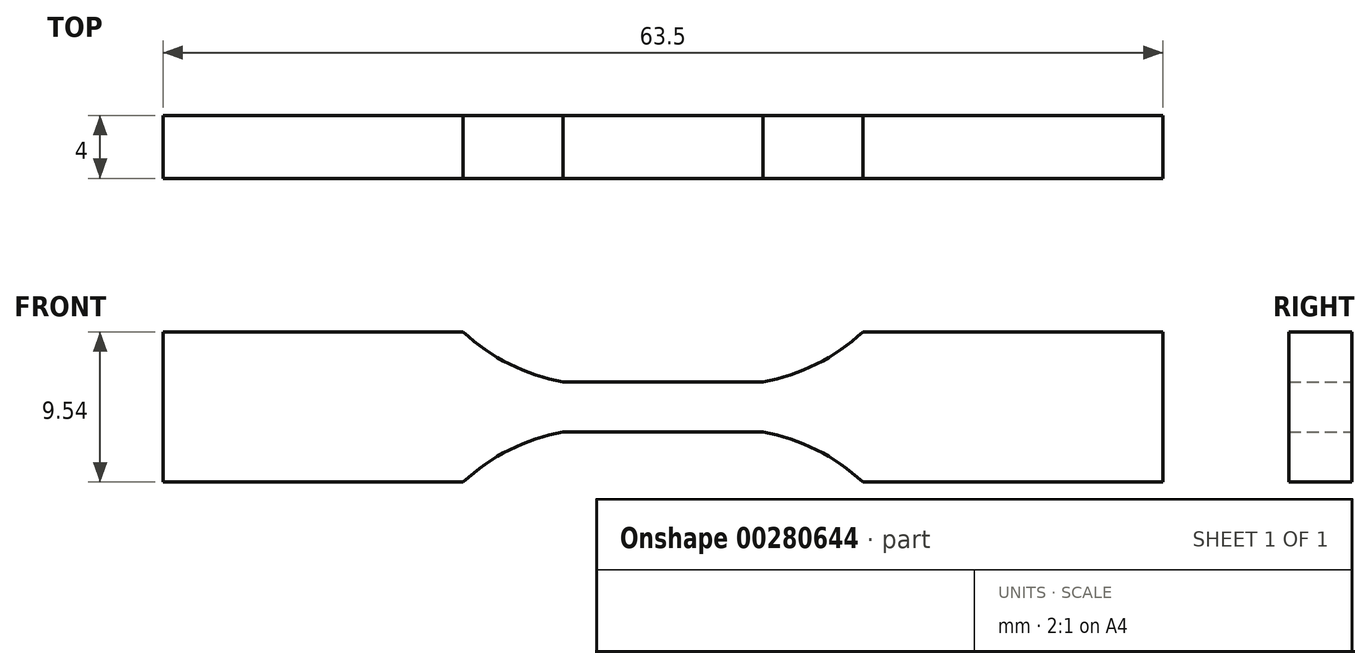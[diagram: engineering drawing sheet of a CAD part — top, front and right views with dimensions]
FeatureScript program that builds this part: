
annotation { "Feature Type Name" : "Feature", "Feature Type Description" : "" }
export const myFeature = defineFeature(function(context is Context, id is Id, definition is map)
    precondition{}
    {
        {
            var Q0;
            Q0=qCreatedBy(makeId("Front.planeOp"),FACE);
            var sketch = newSketch(context, id + "F0", { "sketchPlane" : qUnion([Q0])});
            skLineSegment(sketch, "E0", {"start": v(0, 1.6) * mm, "end": v(6.35, 1.6) * mm});
            skArc(sketch, "E1", {"start": v(6.35, 1.59) * mm, "mid": v(9.75, 2.72) * mm, "end": v(12.7, 4.76) * mm});
            skLineSegment(sketch, "E2", {"start": v(12.7, 4.76) * mm, "end": v(31.75, 4.76) * mm});
            skLineSegment(sketch, "E3.MirrorCS", {"start": v(12.7, -4.76) * mm, "end": v(31.75, -4.76) * mm});
            skLineSegment(sketch, "E4.MirrorCS", {"start": v(0, -1.6) * mm, "end": v(6.35, -1.6) * mm});
            skArc(sketch, "E5.MirrorCS", {"start": v(6.35, -1.59) * mm, "mid": v(9.75, -2.72) * mm, "end": v(12.7, -4.77) * mm});
            skLineSegment(sketch, "E6.MirrorCS", {"start": v(0, -1.6) * mm, "end": v(-6.35, -1.6) * mm});
            skLineSegment(sketch, "E7.MirrorCS", {"start": v(0, 1.6) * mm, "end": v(-6.35, 1.6) * mm});
            skArc(sketch, "E8.MirrorCS", {"start": v(-6.35, -1.59) * mm, "mid": v(-9.75, -2.72) * mm, "end": v(-12.7, -4.77) * mm});
            skLineSegment(sketch, "E9.MirrorCS", {"start": v(-12.7, -4.76) * mm, "end": v(-31.75, -4.76) * mm});
            skLineSegment(sketch, "E10.MirrorCS", {"start": v(-12.7, 4.77) * mm, "end": v(-31.75, 4.76) * mm});
            skArc(sketch, "E11.MirrorCS", {"start": v(-6.35, 1.59) * mm, "mid": v(-9.75, 2.72) * mm, "end": v(-12.7, 4.77) * mm});
            skLineSegment(sketch, "E12", {"start": v(-31.75, 4.76) * mm, "end": v(-31.75, -4.76) * mm});
            skLineSegment(sketch, "E13", {"start": v(31.75, -4.76) * mm, "end": v(31.75, 4.76) * mm});
            skSolve(sketch);
        }
        {
            var Q0;
            Q0 = qSketchRegion(id + "F0", true);
            extrude(context, id + "F1", {"entities" : qUnion([Q0]), "endBound" : BoundingType.SYMMETRIC, "depth" : 4 * mm});
        }
    });
